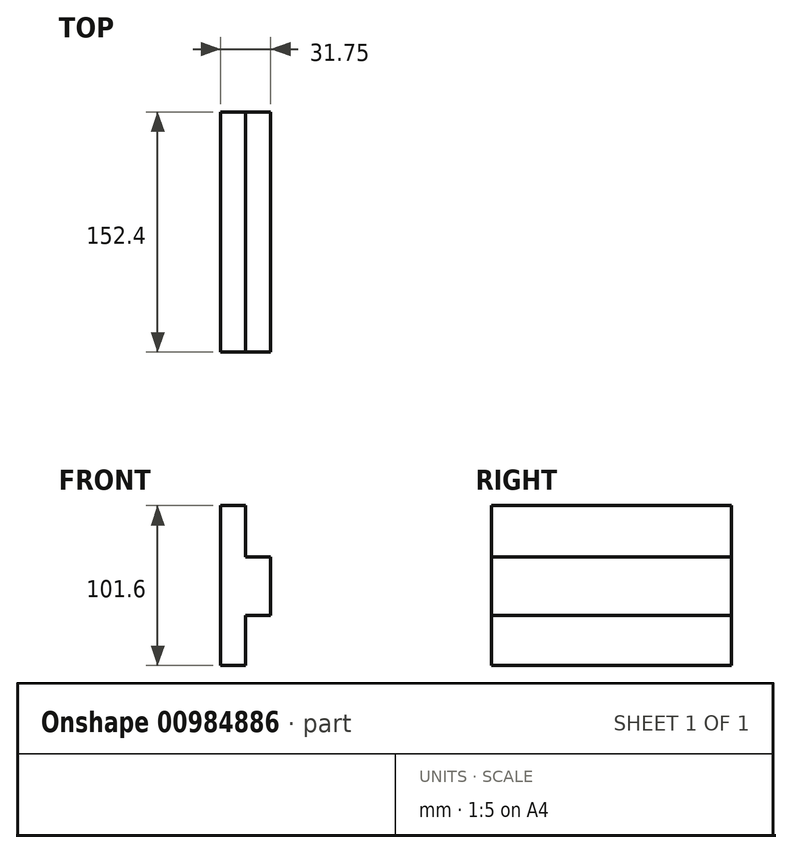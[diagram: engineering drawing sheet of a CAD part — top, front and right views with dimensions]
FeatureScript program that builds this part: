
annotation { "Feature Type Name" : "Feature", "Feature Type Description" : "" }
export const myFeature = defineFeature(function(context is Context, id is Id, definition is map)
    precondition{}
    {
        {
            var Q0;
            Q0=qCreatedBy(makeId("Front.planeOp"),FACE);
            var sketch = newSketch(context, id + "F0", { "sketchPlane" : qUnion([Q0])});
            skLineSegment(sketch, "E0.bottom", {"start": v(-44.9, 51.35) * mm, "end": v(-13.15, 51.35) * mm});
            skLineSegment(sketch, "E0.top", {"start": v(-44.9, -50.25) * mm, "end": v(-13.15, -50.25) * mm});
            skLineSegment(sketch, "E0.left", {"start": v(-44.9, 51.35) * mm, "end": v(-44.9, -50.25) * mm});
            skLineSegment(sketch, "E0.right", {"start": v(-13.15, 51.35) * mm, "end": v(-13.15, -50.25) * mm});
            skLineSegment(sketch, "E1.bottom", {"start": v(72.64, 50.98) * mm, "end": v(72.64, 50.98) * mm});
            skLineSegment(sketch, "E1.top", {"start": v(72.64, 53.09) * mm, "end": v(72.64, 53.09) * mm});
            skLineSegment(sketch, "E1.left", {"start": v(72.64, 50.98) * mm, "end": v(72.64, 53.09) * mm});
            skLineSegment(sketch, "E1.right", {"start": v(72.64, 50.98) * mm, "end": v(72.64, 53.09) * mm});
            skLineSegment(sketch, "E2", {"start": v(-29.03, 51.35) * mm, "end": v(-29.03, 18.8) * mm});
            skLineSegment(sketch, "E3", {"start": v(-29.03, 51.35) * mm, "end": v(-13.15, 51.35) * mm});
            skLineSegment(sketch, "E4", {"start": v(-29.03, 18.8) * mm, "end": v(-13.15, 18.8) * mm});
            skLineSegment(sketch, "E5", {"start": v(-29.03, -50.25) * mm, "end": v(-29.03, -18.5) * mm});
            skLineSegment(sketch, "E6", {"start": v(-29.03, -18.5) * mm, "end": v(-13.15, -18.5) * mm});
            skSolve(sketch);
        }
        {
            var Q0;
            {var subQ3=sQuery(id+"F0.wireOp",EDGE,"E0.left");Q0=makeQuery(id+"F0.imprint","IMPRINT",FACE,{"disambiguationData":[TD([[makeQuery(id+"F0.imprint","IMPRINT",EDGE,{"derivedFrom":subQ3}),1.0]])]});}
            extrude(context, id + "F1", {"entities" : qUnion([Q0]), "depth" : 152.4 * mm, "offsetDistance" : 25.4 * mm});
        }
    });
